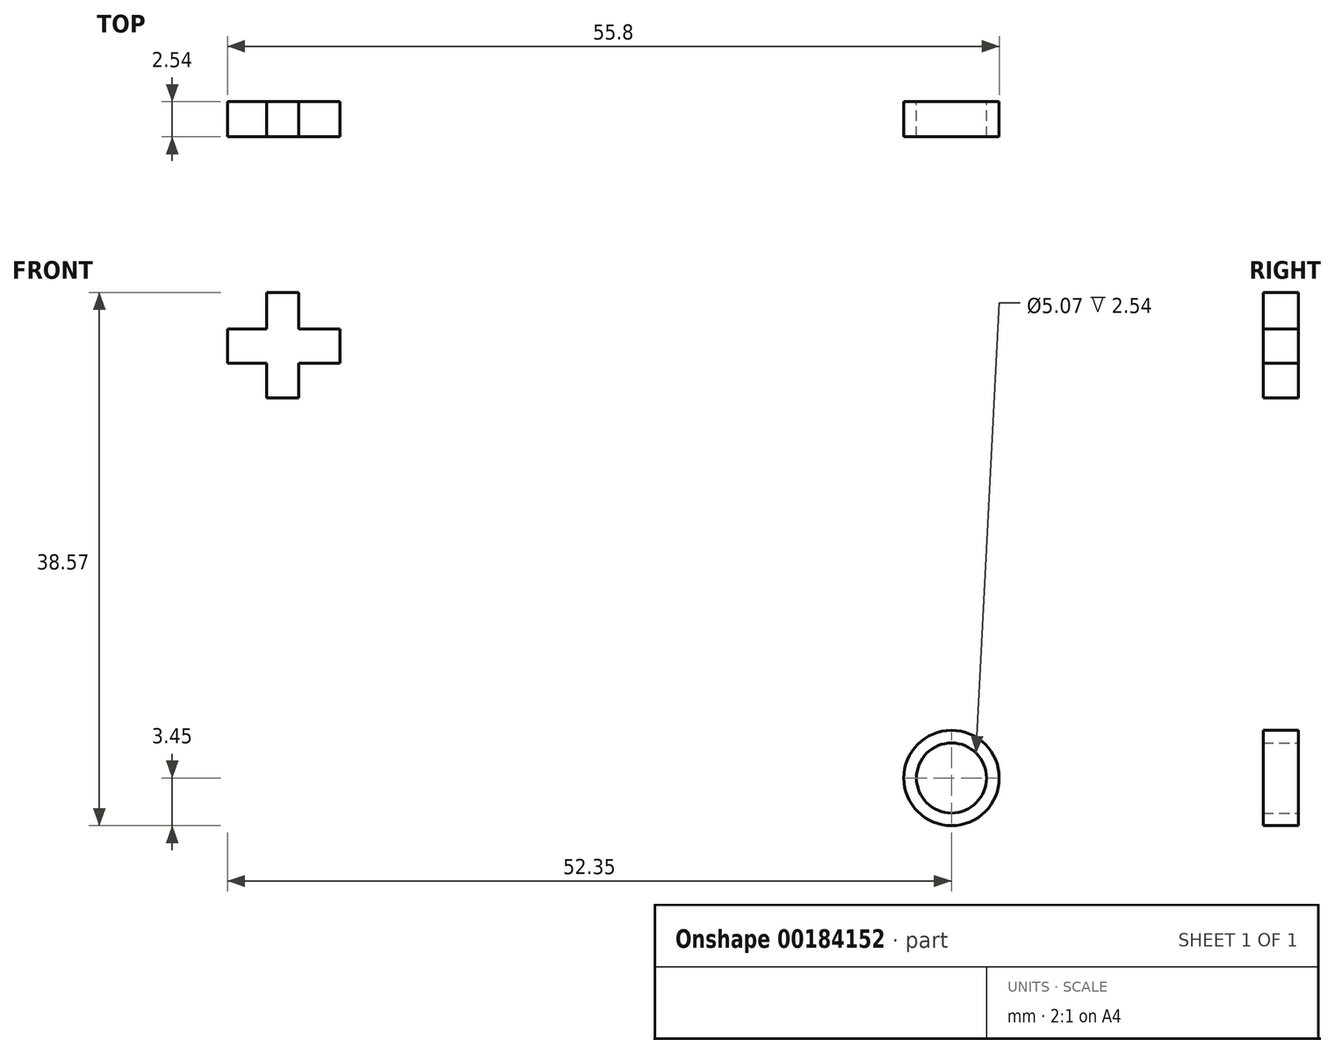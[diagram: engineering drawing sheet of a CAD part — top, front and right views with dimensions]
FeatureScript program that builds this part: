
annotation { "Feature Type Name" : "Feature", "Feature Type Description" : "" }
export const myFeature = defineFeature(function(context is Context, id is Id, definition is map)
    precondition{}
    {
        {
            var Q0;
            Q0=qCreatedBy(makeId("Front.planeOp"),FACE);
            var sketch = newSketch(context, id + "F0", { "sketchPlane" : qUnion([Q0])});
            skCircle(sketch, "E0", {"center": v(0, 0) * mm, "radius": 3.45 * mm});
            skSolve(sketch);
        }
        {
            var Q0;
            Q0 = qSketchRegion(id + "F0", true);
            extrude(context, id + "F1", {"entities" : qUnion([Q0]), "depth" : 2.54 * mm});
        }
        {
            var Q0;
            Q0=qCreatedBy(makeId("Front.planeOp"),FACE);
            var sketch = newSketch(context, id + "F2", { "sketchPlane" : qUnion([Q0])});
            skCircle(sketch, "E1", {"center": v(0, 0) * mm, "radius": 2.53 * mm});
            skSolve(sketch);
        }
        {
            var Q0;
            Q0=makeQuery(id+"F2.imprint","IMPRINT",FACE,{"disambiguationData":[TD([[makeQuery(id+"F2.imprint","IMPRINT",EDGE,{"derivedFrom":sQuery(id+"F2.wireOp",EDGE,"E1")}),1.0]])]});
            extrude(context, id + "F3", {"entities" : qUnion([Q0]), "operationType" : NewBodyOperationType.REMOVE, "depth" : 25.15 * mm});
        }
        {
            var Q0;
            Q0=qCreatedBy(makeId("Front.planeOp"),FACE);
            var sketch = newSketch(context, id + "F4", { "sketchPlane" : qUnion([Q0])});
            skLineSegment(sketch, "E2.bottom", {"start": v(-52.35, 32.47) * mm, "end": v(-44.4, 32.47) * mm});
            skLineSegment(sketch, "E2.top", {"start": v(-52.35, 31.3) * mm, "end": v(-44.4, 31.3) * mm});
            skLineSegment(sketch, "E2.left", {"start": v(-52.35, 32.47) * mm, "end": v(-52.35, 31.3) * mm});
            skLineSegment(sketch, "E2.right", {"start": v(-44.4, 32.47) * mm, "end": v(-44.4, 31.3) * mm});
            skLineSegment(sketch, "E3.bottom", {"start": v(-47.21, 27.5) * mm, "end": v(-49.53, 27.5) * mm});
            skLineSegment(sketch, "E3.top", {"start": v(-47.21, 35.12) * mm, "end": v(-49.53, 35.12) * mm});
            skLineSegment(sketch, "E3.left", {"start": v(-47.21, 27.5) * mm, "end": v(-47.21, 35.12) * mm});
            skLineSegment(sketch, "E3.right", {"start": v(-49.53, 27.5) * mm, "end": v(-49.53, 35.12) * mm});
            skPoint(sketch, "E3.middle", {"position": v(-48.37, 31.3) * mm});
            skLineSegment(sketch, "E4.bottom", {"start": v(-52.35, 32.47) * mm, "end": v(-44.23, 32.47) * mm});
            skLineSegment(sketch, "E4.top", {"start": v(-52.35, 29.98) * mm, "end": v(-44.23, 29.98) * mm});
            skLineSegment(sketch, "E4.left", {"start": v(-52.35, 32.47) * mm, "end": v(-52.35, 29.98) * mm});
            skLineSegment(sketch, "E4.right", {"start": v(-44.23, 32.47) * mm, "end": v(-44.23, 29.98) * mm});
            skSolve(sketch);
        }
        {
            var Q0;
            Q0 = qSketchRegion(id + "F4", true);
            extrude(context, id + "F5", {"entities" : qUnion([Q0]), "depth" : 2.54 * mm});
        }
    });
